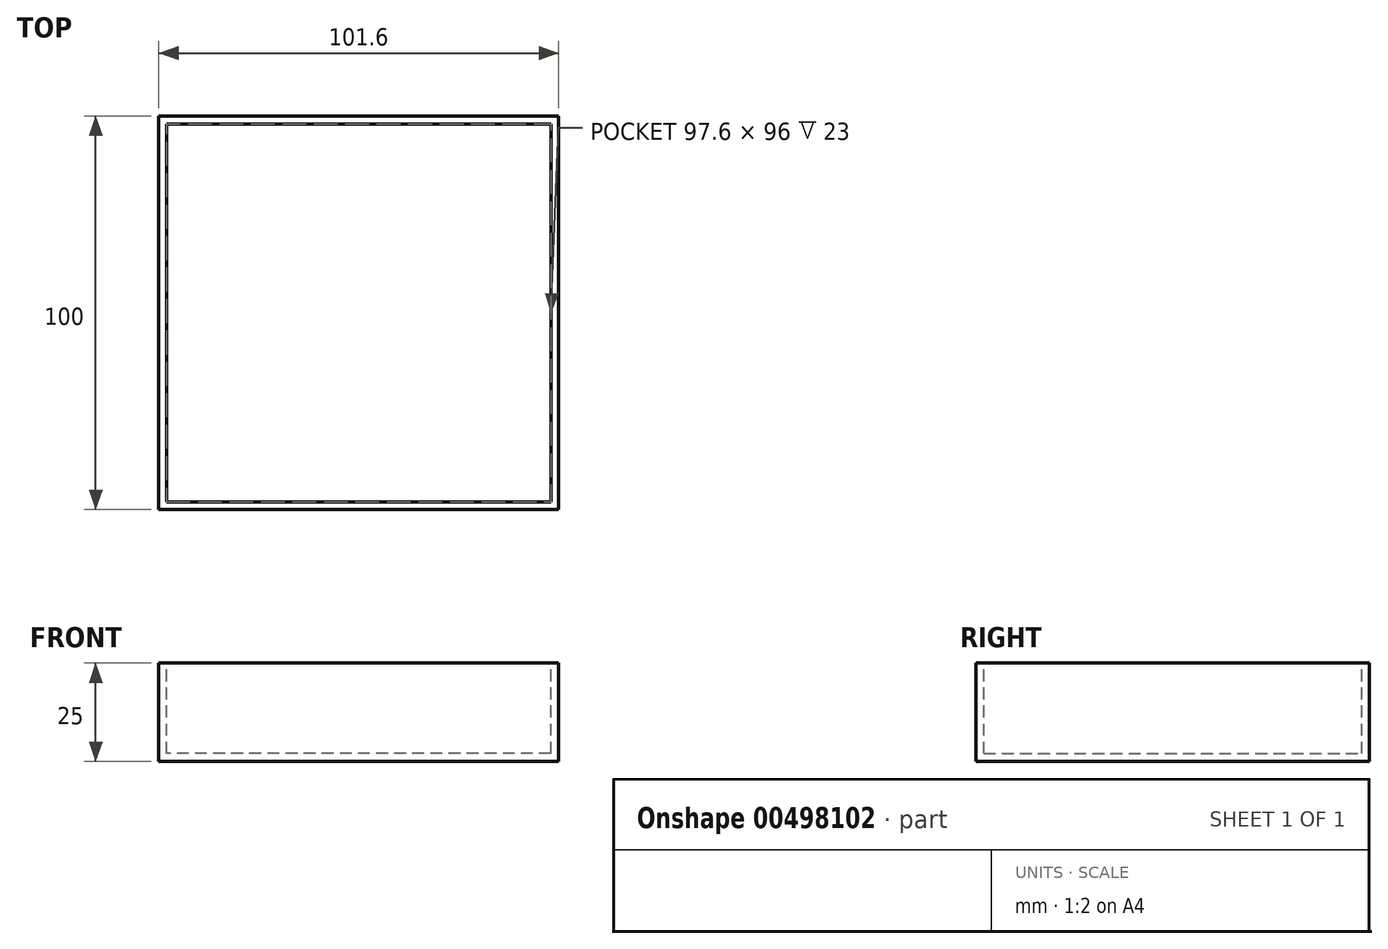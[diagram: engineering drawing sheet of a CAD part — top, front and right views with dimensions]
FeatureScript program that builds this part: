
annotation { "Feature Type Name" : "Feature", "Feature Type Description" : "" }
export const myFeature = defineFeature(function(context is Context, id is Id, definition is map)
    precondition{}
    {
        {
            assignVariable(context, id + "F0", {"name" : "stageheight", "anyValue" : 25});
        }
        {
            assignVariable(context, id + "F1", {"name" : "wallthick", "anyValue" : 2});
        }
        {
            var Q0;
            Q0=qCreatedBy(makeId("Top.planeOp"),FACE);
            var sketch = newSketch(context, id + "F2", { "sketchPlane" : qUnion([Q0])});
            skLineSegment(sketch, "E0.bottom", {"start": v(50.8, -50) * mm, "end": v(-50.8, -50) * mm});
            skLineSegment(sketch, "E0.top", {"start": v(50.8, 50) * mm, "end": v(-50.8, 50) * mm});
            skLineSegment(sketch, "E0.left", {"start": v(50.8, -50) * mm, "end": v(50.8, 50) * mm});
            skLineSegment(sketch, "E0.right", {"start": v(-50.8, -50) * mm, "end": v(-50.8, 50) * mm});
            skPoint(sketch, "E0.middle", {"position": v(0, 0) * mm});
            skSolve(sketch);
        }
        {
            var Q0;
            Q0=makeQuery(id+"F2.imprint","IMPRINT",FACE,{"disambiguationData":[TD([[makeQuery(id+"F2.imprint","IMPRINT",EDGE,{"derivedFrom":sQuery(id+"F2.wireOp",EDGE,"E0.bottom")}),-1.0]])]});
            extrude(context, id + "F3", {"entities" : qUnion([Q0]), "depth" : 25 * mm});
        }
        {
            var Q0;
            Q0=makeQuery(id+"F3.opExtrude","CAP_FACE",FACE,{"disambiguationData":[OSD([sQuery(id+"F2.wireOp",EDGE,"E0.bottom"),sQuery(id+"F2.wireOp",EDGE,"E0.top"),sQuery(id+"F2.wireOp",EDGE,"E0.left"),sQuery(id+"F2.wireOp",EDGE,"E0.right")])],"isStart":false});
            var sketch = newSketch(context, id + "F4", { "sketchPlane" : qUnion([Q0])});
            skLineSegment(sketch, "E1.bottom", {"start": v(48.8, -48) * mm, "end": v(-48.8, -48) * mm});
            skLineSegment(sketch, "E1.top", {"start": v(48.8, 48) * mm, "end": v(-48.8, 48) * mm});
            skLineSegment(sketch, "E1.left", {"start": v(48.8, -48) * mm, "end": v(48.8, 48) * mm});
            skLineSegment(sketch, "E1.right", {"start": v(-48.8, -48) * mm, "end": v(-48.8, 48) * mm});
            skPoint(sketch, "E1.middle", {"position": v(0, 0) * mm});
            skLineSegment(sketch, "E2", {"start": v(0, 48) * mm, "end": v(0, 50) * mm, "construction": true});
            skLineSegment(sketch, "E3", {"start": v(48.8, 0) * mm, "end": v(50.8, 0) * mm, "construction": true});
            skSolve(sketch);
        }
        {
            var Q0;
            Q0 = qSketchRegion(id + "F4", true);
            extrude(context, id + "F5", {"entities" : qUnion([Q0]), "operationType" : NewBodyOperationType.REMOVE, "oppositeDirection" : true, "depth" : (getVariable(context, 'stageheight') - getVariable(context, 'wallthick')) * mm});
        }
    });
